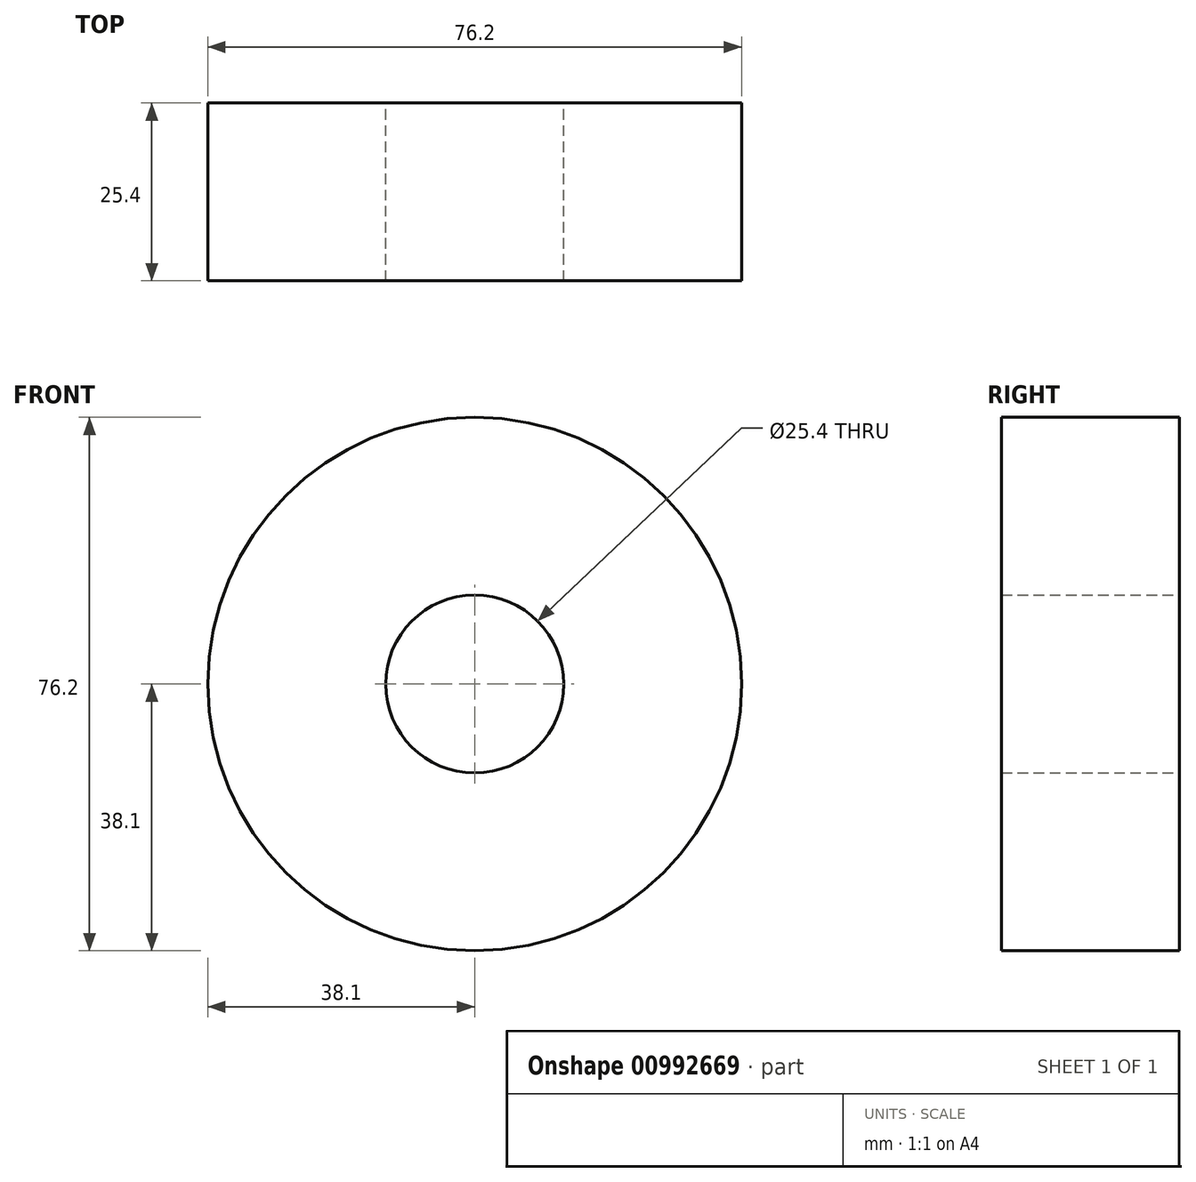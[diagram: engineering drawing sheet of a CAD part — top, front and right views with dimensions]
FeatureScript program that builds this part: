
annotation { "Feature Type Name" : "Feature", "Feature Type Description" : "" }
export const myFeature = defineFeature(function(context is Context, id is Id, definition is map)
    precondition{}
    {
        {
            var Q0;
            Q0=qCreatedBy(makeId("Front.planeOp"),FACE);
            var sketch = newSketch(context, id + "F0", { "sketchPlane" : qUnion([Q0])});
            skCircle(sketch, "E0", {"center": v(0, 0) * mm, "radius": 38.1 * mm});
            skCircle(sketch, "E1", {"center": v(0, 0) * mm, "radius": 12.7 * mm});
            skSolve(sketch);
        }
        {
            var Q0;
            Q0=makeQuery(id+"F0.imprint","IMPRINT",FACE,{"disambiguationData":[TD([[makeQuery(id+"F0.imprint","IMPRINT",EDGE,{"derivedFrom":sQuery(id+"F0.wireOp",EDGE,"E0")}),1.0]])]});
            extrude(context, id + "F1", {"entities" : qUnion([Q0]), "depth" : 25.4 * mm, "offsetDistance" : 25.4 * mm});
        }
    });
